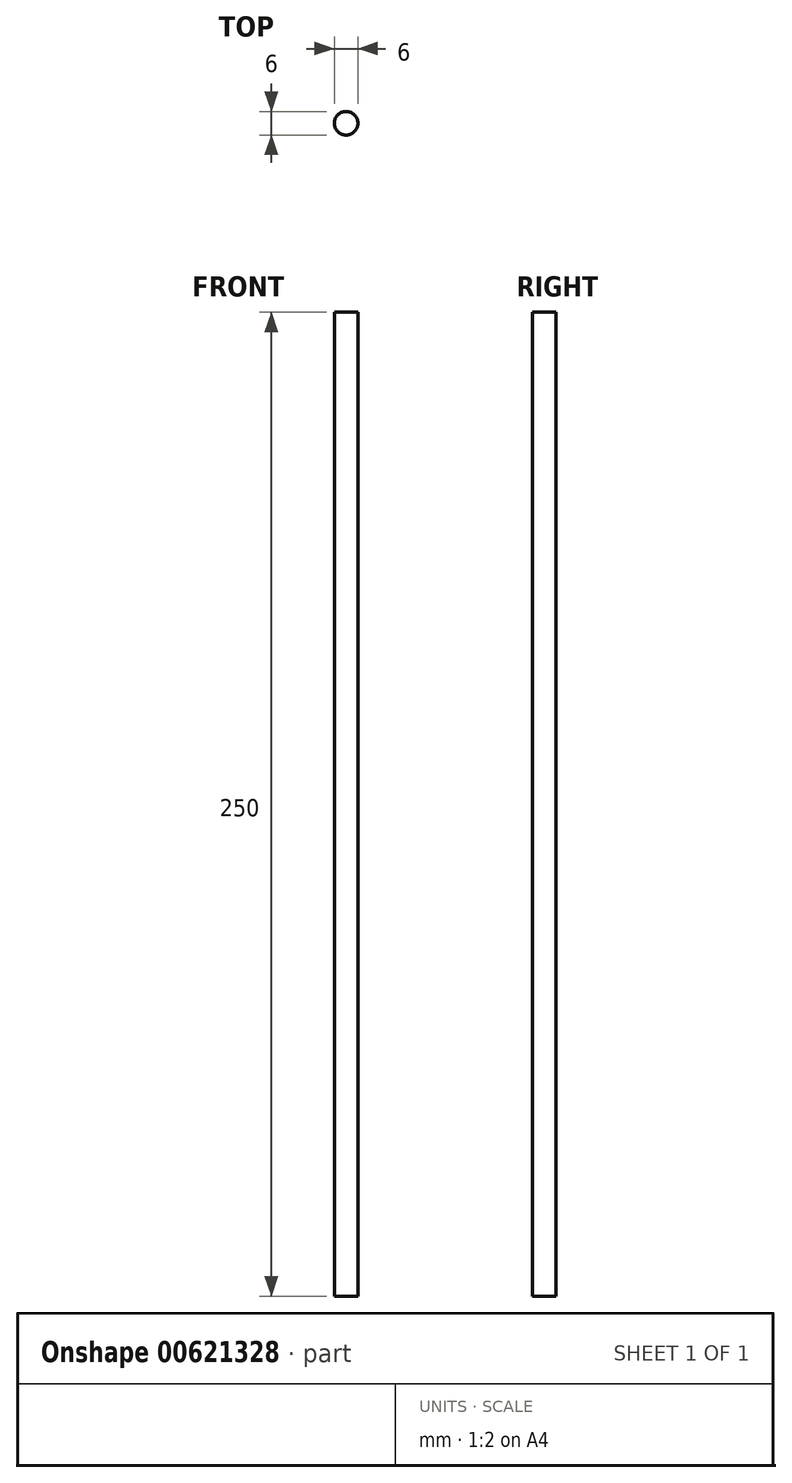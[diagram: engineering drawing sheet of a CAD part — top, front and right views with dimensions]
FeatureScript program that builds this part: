
annotation { "Feature Type Name" : "Feature", "Feature Type Description" : "" }
export const myFeature = defineFeature(function(context is Context, id is Id, definition is map)
    precondition{}
    {
        {
            var Q0;
            Q0=qCreatedBy(makeId("Top.planeOp"),FACE);
            var sketch = newSketch(context, id + "F0", { "sketchPlane" : qUnion([Q0])});
            skCircle(sketch, "E0", {"center": v(0, 0) * mm, "radius": 3 * mm});
            skSolve(sketch);
        }
        {
            var Q0;
            Q0 = qSketchRegion(id + "F0", true);
            extrude(context, id + "F1", {"entities" : qUnion([Q0]), "depth" : 250 * mm, "offsetDistance" : 25 * mm});
        }
    });
